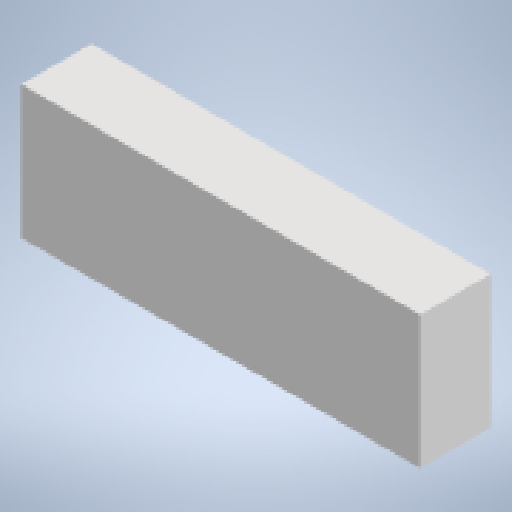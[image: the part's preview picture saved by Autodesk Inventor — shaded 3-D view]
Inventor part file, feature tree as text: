
AUTODESK INVENTOR PART (.ipt)
format: ipt  version: 2024.2 (Build 282272000, 272)  size: 111,104 bytes
history: native  units: mm
features: extrude x1, sketch x1
ambient origin geometry x8: Origin, YZ Plane, XZ Plane, XY Plane, X Axis, Y Axis, Z Axis, Center Point
bodies: Solid1 (feature_tree)
feature tree (2):
  extrude  "Extrusion1"  Depth=17.0mm
  sketch  "Sketch1"  dims[d0=51.0mm d1=17.0mm d2=9.0mm d3=0.0mm]
